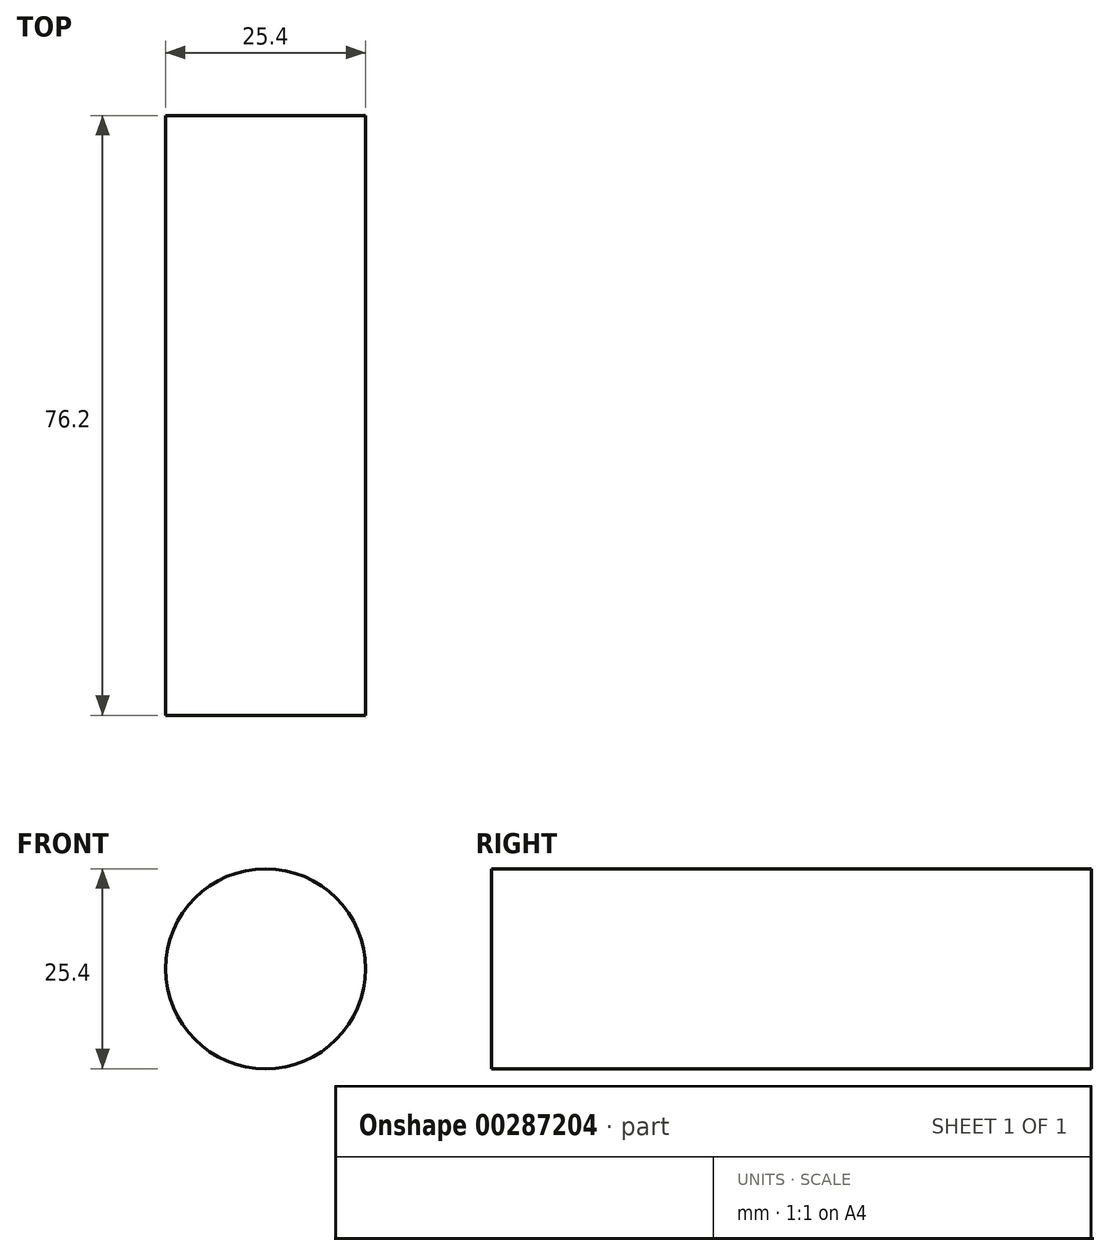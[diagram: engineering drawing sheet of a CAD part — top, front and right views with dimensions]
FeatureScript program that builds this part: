
annotation { "Feature Type Name" : "Feature", "Feature Type Description" : "" }
export const myFeature = defineFeature(function(context is Context, id is Id, definition is map)
    precondition{}
    {
        {
            var Q0;
            Q0=qCreatedBy(makeId("Front.planeOp"),FACE);
            var sketch = newSketch(context, id + "F0", { "sketchPlane" : qUnion([Q0])});
            skCircle(sketch, "E0", {"center": v(-38.2, 33.23) * mm, "radius": 12.7 * mm});
            skSolve(sketch);
        }
        {
            var Q0;
            Q0 = qSketchRegion(id + "F0", true);
            extrude(context, id + "F1", {"entities" : qUnion([Q0]), "depth" : 76.2 * mm});
        }
    });
